FCSTD DOCUMENT  (FreeCAD 0.21R33771 (Git))
Label: curve_test2
License: All rights reserved
LicenseURL: http://en.wikipedia.org/wiki/All_rights_reserved
objects: Sketcher::SketchObject×3, PartDesign::Body×1
note: 4 computed .brp shape members not serialized (recipe doc carries the construction recipe); baked Part::Feature solids carry a one-line shape summary decoded from their .brp

FEATURE [Sketcher::SketchObject] Sketch
  FullyConstrained = false
  MapMode = 5
  Support = -> [XY_Plane]
  sketch-geometry (3):
    g0: LineSegment StartX=-50 StartY=0 StartZ=0 EndX=-50 EndY=26.988 EndZ=0
    g1: ArcOfCircle CenterX=0 CenterY=26.988 CenterZ=0 NormalX=0 NormalY=0 NormalZ=1 AngleXU=0 Radius=50 StartAngle=6.27743 EndAngle=9.42478
    g2: LineSegment StartX=49.9992 StartY=26.7003 StartZ=0 EndX=49.9992 EndY=0 EndZ=0
  constraints (8):
    c: PointOnObject(g0,g-1)
    c: Vertical(g0)
    c: Tangent(g0,g1) = 1.5708
    c: Coincident(g1,g2)
    c: PointOnObject(g2,g-1)
    c: Vertical(g2)
    c: PointOnObject(g1,g-2)
    c: DistanceX(g0,g-1) = 50
FEATURE [Sketcher::SketchObject] Sketch001
  FullyConstrained = false
  MapMode = 5
  Placement = pos=(0,0,0) rot=(1,0,0;1.5708rad)
  Support = -> [XZ_Plane]
  sketch-geometry (3):
    g0: LineSegment StartX=-50 StartY=0 StartZ=0 EndX=-50 EndY=-15.6809 EndZ=0
    g1: ArcOfCircle CenterX=0.00101982 CenterY=-15.6809 CenterZ=0 NormalX=0 NormalY=0 NormalZ=1 AngleXU=0 Radius=50.001 StartAngle=3.14159 EndAngle=6.27415
    g2: LineSegment StartX=50 StartY=-16.1325 StartZ=0 EndX=50 EndY=0 EndZ=0
  constraints (7):
    c: PointOnObject(g0,g-1)
    c: Vertical(g0)
    c: Tangent(g0,g1) = -1.5708
    c: Coincident(g1,g2)
    c: Vertical(g2)
    c: DistanceX(g0,g2) = 100
    c: Symmetric(g2,g0,g-2)
FEATURE [Sketcher::SketchObject] Sketch002
  ExternalGeometry = -> [Sketch,Sketch001]
  FullyConstrained = false
  MapMode = 5
  Placement = pos=(0,0,0) rot=(0.57735,0.57735,0.57735;2.0944rad)
  Support = -> [YZ_Plane]
  sketch-geometry (3):
    g0: LineSegment StartX=0 StartY=-65.6819 StartZ=0 EndX=32.0408 EndY=-65.6819 EndZ=0
    g1: ArcOfCircle CenterX=32.0408 CenterY=-20.7184 CenterZ=0 NormalX=0 NormalY=0 NormalZ=1 AngleXU=0 Radius=44.9636 StartAngle=4.71239 EndAngle=6.31016
    g2: LineSegment StartX=76.988 StartY=-19.5058 StartZ=0 EndX=76.988 EndY=0 EndZ=0
  constraints (6):
    c: Coincident(g-4,g0)
    c: Horizontal(g0)
    c: Tangent(g0,g1) = -1.5708
    c: Coincident(g1,g2)
    c: Coincident(g2,g-3)
    c: Vertical(g2)
FEATURE [PartDesign::Body] Body
  Group = -> [Sketch,Sketch001,Sketch002]
  Origin = -> Origin
